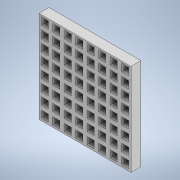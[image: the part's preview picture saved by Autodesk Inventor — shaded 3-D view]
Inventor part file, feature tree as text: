
AUTODESK INVENTOR PART (.ipt)
format: ipt  version: 2020.1 (Build 241239000, 239)  size: 1,664,512 bytes
history: native  units: in
note: dims shown in document units (in); Inventor stores cm internally (conversion verified against a paired STEP export)
features: extrude x5, sketch x2
ambient origin geometry x8: Origin, YZ Plane, XZ Plane, XY Plane, X Axis, Y Axis, Z Axis, Center Point
bodies: Solid1 (feature_tree)
feature tree (7):
  sketch  "Sketch1"  dims[d34=0.2756in d35=0.0in d36=0.0394in]
  extrude  "Extrusion1"  Depth=0.0394in
  extrude  "Extrusion2"  Depth=0.1378in TaperAngle=0.0deg
  extrude  "Extrusion3"  Depth=0.1378in TaperAngle=0.0deg
  extrude  "Extrusion4"  Depth=0.0984in TaperAngle=0.0deg
  extrude  "Extrusion5"  Depth=0.0197in
  sketch  "Sketch2"  dims[d39=3.1496in d41=0.3198in d42=3.1496in d44=0.3198in d47=0.1378in d48=0.0in d49=0.1378in d50=0.0in d51=0.0984in d52=0.0in d53=0.0197in d54=3.1496in d56=0.3198in d57=3.1496in d59=0.3198in d62=0.1378in d63=0.0in d64=0.1575in d65=0.1575in d37=0.0344in]
